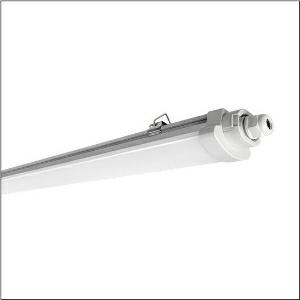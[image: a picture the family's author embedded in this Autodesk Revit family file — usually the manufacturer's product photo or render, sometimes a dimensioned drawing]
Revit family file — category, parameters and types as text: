
# Revit family: monsun_41_51fk20mn460a003
name_source: partatom
category: Lighting Fixtures
units: mm (PartAtom-declared; Revit-internal decimal feet)

## family parameters
Cut with Voids When Loaded = No
Host = Face
Light Source = No
Part Type = Normal
Room Calculation Point = No
Round Connector Dimension = Use Diameter
Shared = No

## types (1)
- --- (1 x LED, 6000 lm, 46 W, 4000K)
    Apparent Load = 46 VA
    CIE Flux Codes = 44 74 91 91 100
    Color Rendering = 80
    Color Temperature = 4000K
    Default Elevation = 1800 mm
    Description = Monsun 41, damp-proof luminaire, primary optical cover: diffuser, of PC, frosted, light emission: direct distribution, primary light characteristic: symmetric, installation type: suspended mounting, surface-mounted, LED, rated luminous flux: 6.000lm, luminous efficacy: 130lm/W, light colour: 840, colour temperature: 4000K, control gear: ON/OFF Multilumen, with terminal, 3-pole, through-wiring: 3x 1.5mm², mains connection: 220..240V, AC, 50/60Hz, rated input power: 46W, housing, luminaire housing, of PC, grey, length: 1.500mm, width: 79mm, height: 52mm, end cap, of PC, grey, ceiling mounting element, of stainless steel (V2A), protection rating (complete): IP65, insulation class (complete): insulation class II (safety insulation), certification: CE, UKCA, protection symbol: D, impact resistance: IK08, permissible operating ambient temperature: -20..+35°C, corresponds to IFS (International Featured Standards) requirements for safety and quality in the food industry, contact your sales advisor before using the luminaires in applications with unclear chemical exposure, large temperature fluctuations or condensation-forming humidity, packaging unit: 1 piece
    Height = 54 mm
    Lamp = 1 x LED
    Lamp Light Flux = 6000 lm
    Lamp Power = 46 W
    Lamp count = 1
    Length = 1500 mm
    Luminous efficacy = 130 lm/W
    Manufacturer = Siteco
    ModVariant = No
    Model = 51FK20MN460A003
    Mounting Place = Ceiling
    Mounting Type = Surface mounted
    Number of Poles = 1
    OnlyDefault = Yes
    Power Factor = 1
    Product Name = Monsun 41
    Product group = damp-proof luminaire
    ProductGroupID = 300
    Protection Class = Protection class II
    Protection Degree = IP 65
    RLX_Detail_Level = 1
    RLX_Emergency_Light_Flux = 0 lm
    RLX_Emergency_Type = 0
    RLX_Emergency_Type_DB = No
    RlxData = <blob elided: 29005 chars, md5=da5282c6>
    Socket = socket
    Standby Power = 0 W
    System Light Flux = 6000 lm
    System Power = 46 W
    Type Comments = factory setting: luminous flux: 100 % | (HIGH)
    Type Image = l_1007037.jpg
    URL = http://relux.com
    VarID = @adj_174175
    Voltage = 0 V
    Weight = 0.00 kg
    Width = 79 mm

## geometry (parser evidence)
native form markers: Blend x4, Sweep x10
no freeform markers — native parametric forms only
